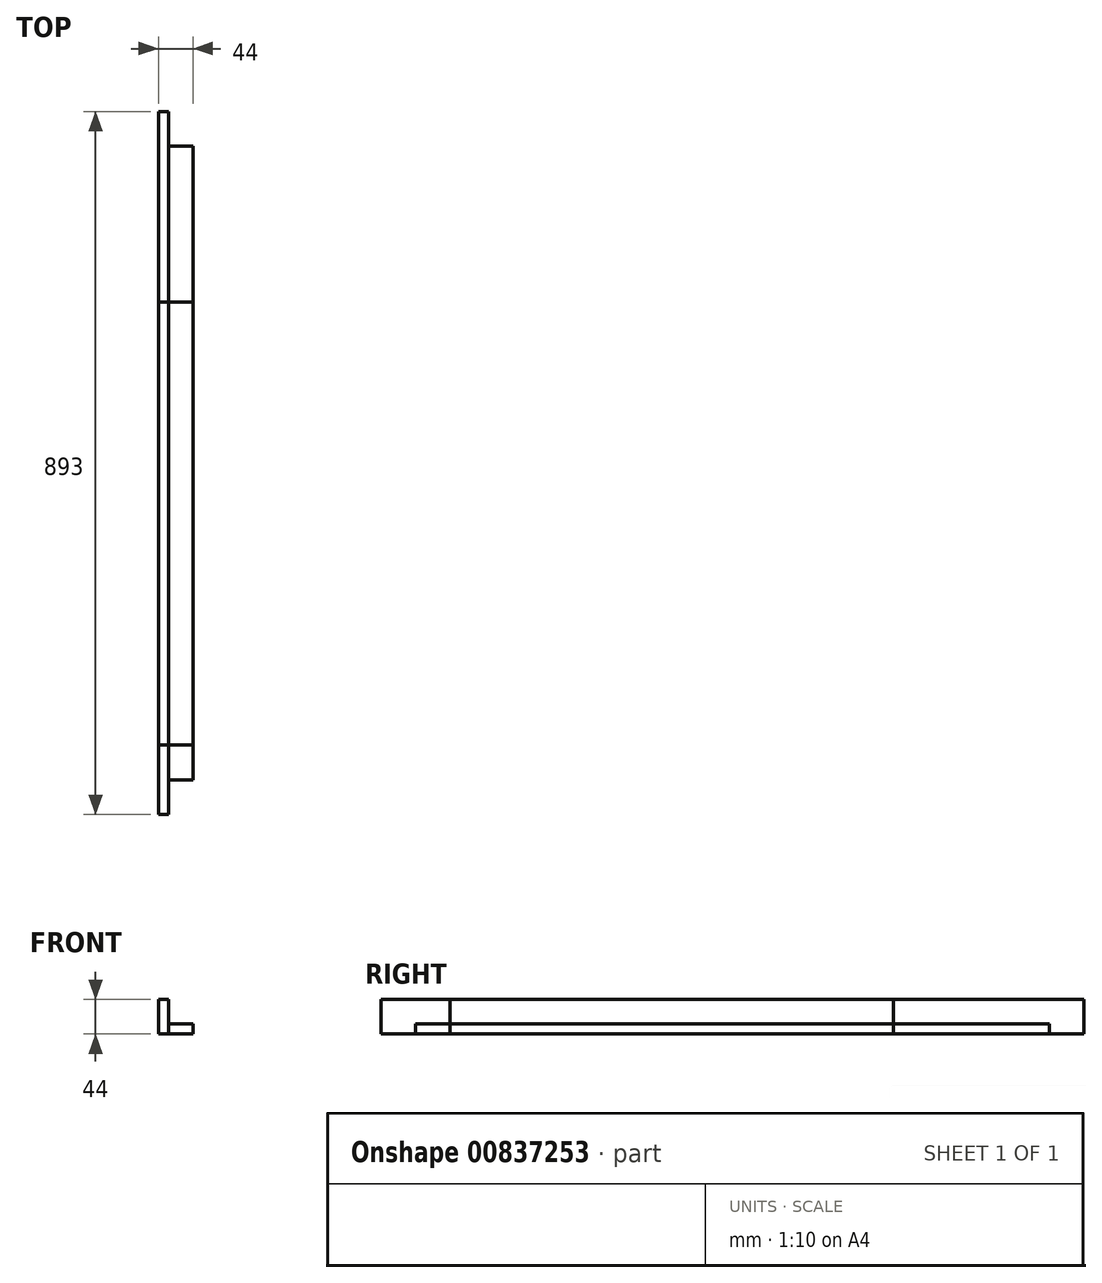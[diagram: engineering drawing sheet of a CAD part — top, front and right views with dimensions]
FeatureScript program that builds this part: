
annotation { "Feature Type Name" : "Feature", "Feature Type Description" : "" }
export const myFeature = defineFeature(function(context is Context, id is Id, definition is map)
    precondition{}
    {
        {
            var Q0;
            Q0=qCreatedBy(makeId("Front.planeOp"),FACE);
            var sketch = newSketch(context, id + "F0", { "sketchPlane" : qUnion([Q0])});
            skLineSegment(sketch, "E0", {"start": v(-22, 22) * mm, "end": v(-22, -22) * mm});
            skLineSegment(sketch, "E1", {"start": v(-22, -22) * mm, "end": v(22, -22) * mm});
            skLineSegment(sketch, "E2", {"start": v(22, -22) * mm, "end": v(22, -9) * mm});
            skLineSegment(sketch, "E3", {"start": v(22, -9) * mm, "end": v(-9, -9) * mm});
            skLineSegment(sketch, "E4", {"start": v(-9, -9) * mm, "end": v(-9, 22) * mm});
            skLineSegment(sketch, "E5", {"start": v(-9, 22) * mm, "end": v(-22, 22) * mm});
            skLineSegment(sketch, "E6", {"start": v(0, 0) * mm, "end": v(0, -22) * mm, "construction": true});
            skLineSegment(sketch, "E7", {"start": v(0, 0) * mm, "end": v(-22, 0) * mm, "construction": true});
            skSolve(sketch);
        }
        {
            var Q0;
            Q0=makeQuery(id+"F0.imprint","IMPRINT",FACE,{"disambiguationData":[TD([[makeQuery(id+"F0.imprint","IMPRINT",EDGE,{"derivedFrom":sQuery(id+"F0.wireOp",EDGE,"E0")}),1.0]])]});
            extrude(context, id + "F1", {"entities" : qUnion([Q0]), "depth" : 893 * mm, "offsetDistance" : 25 * mm});
        }
        {
            var Q0;
            Q0=makeQuery(id+"F0.imprint","IMPRINT",FACE,{"disambiguationData":[TD([[makeQuery(id+"F0.imprint","IMPRINT",EDGE,{"derivedFrom":sQuery(id+"F0.wireOp",EDGE,"E0")}),1.0]])]});
            extrude(context, id + "F2", {"entities" : qUnion([Q0]), "depth" : 805 * mm, "offsetDistance" : 25 * mm});
        }
        {
            var Q0;
            Q0=makeQuery(id+"F0.imprint","IMPRINT",FACE,{"disambiguationData":[TD([[makeQuery(id+"F0.imprint","IMPRINT",EDGE,{"derivedFrom":sQuery(id+"F0.wireOp",EDGE,"E0")}),1.0]])]});
            extrude(context, id + "F3", {"entities" : qUnion([Q0]), "depth" : 242 * mm, "offsetDistance" : 25 * mm});
        }
        {
            var Q0;
            Q0=makeQuery(id+"F1.opExtrude","SWEPT_FACE",FACE,{"disambiguationData":[OSD([sQuery(id+"F0.wireOp",EDGE,"E2")])]});
            var sketch = newSketch(context, id + "F4", { "sketchPlane" : qUnion([Q0])});
            skLineSegment(sketch, "E8.bottom", {"start": v(-893, -22) * mm, "end": v(-849, -22) * mm});
            skLineSegment(sketch, "E8.top", {"start": v(-893, 22) * mm, "end": v(-849, 22) * mm});
            skLineSegment(sketch, "E8.left", {"start": v(-893, -22) * mm, "end": v(-893, 22) * mm});
            skLineSegment(sketch, "E8.right", {"start": v(-849, -22) * mm, "end": v(-849, 22) * mm});
            skLineSegment(sketch, "E9.bottom", {"start": v(0, -22) * mm, "end": v(-44, -22) * mm});
            skLineSegment(sketch, "E9.top", {"start": v(0, 22) * mm, "end": v(-44, 22) * mm});
            skLineSegment(sketch, "E9.left", {"start": v(0, -22) * mm, "end": v(0, 22) * mm});
            skLineSegment(sketch, "E9.right", {"start": v(-44, -22) * mm, "end": v(-44, 22) * mm});
            skSolve(sketch);
        }
        {
            var Q0;
            {var subQ0=sQuery(id+"F4.wireOp",EDGE,"E9.top");Q0=makeQuery(id+"F4.imprint","IMPRINT",FACE,{"disambiguationData":[TD([[makeQuery(id+"F4.imprint","IMPRINT",EDGE,{"derivedFrom":subQ0}),1.0]])]});}
            var Q1;
            {var subQ0=sQuery(id+"F4.wireOp",EDGE,"E9.bottom");Q1=makeQuery(id+"F4.imprint","IMPRINT",FACE,{"disambiguationData":[TD([[makeQuery(id+"F4.imprint","IMPRINT",EDGE,{"derivedFrom":subQ0}),1.0]])]});}
            var Q2;
            {var subQ0=sQuery(id+"F4.wireOp",EDGE,"E8.top");Q2=makeQuery(id+"F4.imprint","IMPRINT",FACE,{"disambiguationData":[TD([[makeQuery(id+"F4.imprint","IMPRINT",EDGE,{"derivedFrom":subQ0}),-1.0]])]});}
            var Q3;
            {var subQ0=sQuery(id+"F4.wireOp",EDGE,"E8.bottom");Q3=makeQuery(id+"F4.imprint","IMPRINT",FACE,{"disambiguationData":[TD([[makeQuery(id+"F4.imprint","IMPRINT",EDGE,{"derivedFrom":subQ0}),1.0]])]});}
            var Q4;
            Q4=makeQuery(id+"F1.opExtrude","SWEPT_FACE",FACE,{"disambiguationData":[OSD([sQuery(id+"F0.wireOp",EDGE,"E4")])]});
            extrude(context, id + "F5", {"entities" : qUnion([Q0, Q1, Q2, Q3]), "operationType" : NewBodyOperationType.REMOVE, "endBound" : BoundingType.UP_TO_SURFACE, "oppositeDirection" : true, "depth" : 25 * mm, "endBoundEntityFace" : qUnion([Q4]), "offsetDistance" : 25 * mm});
        }
    });
